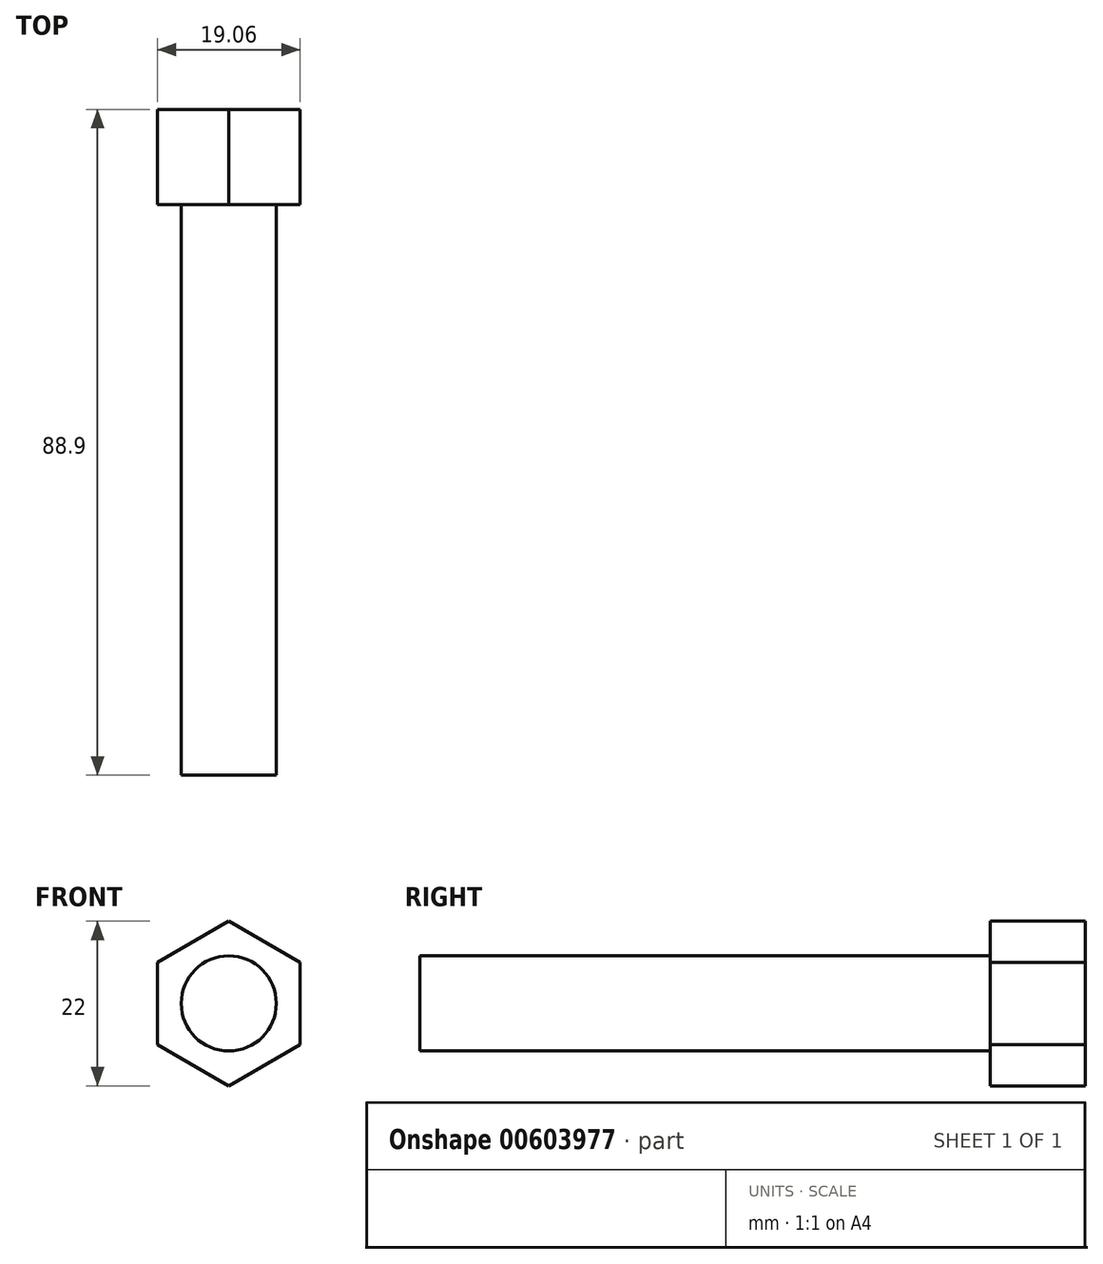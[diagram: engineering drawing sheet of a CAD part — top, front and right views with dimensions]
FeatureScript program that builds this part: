
annotation { "Feature Type Name" : "Feature", "Feature Type Description" : "" }
export const myFeature = defineFeature(function(context is Context, id is Id, definition is map)
    precondition{}
    {
        {
            var Q0;
            Q0=qCreatedBy(makeId("Front.planeOp"),FACE);
            var sketch = newSketch(context, id + "F0", { "sketchPlane" : qUnion([Q0])});
            skCircle(sketch, "E0", {"center": v(0, 0) * mm, "radius": 6.35 * mm});
            skSolve(sketch);
        }
        {
            var Q0;
            Q0 = qSketchRegion(id + "F0", true);
            extrude(context, id + "F1", {"entities" : qUnion([Q0]), "depth" : 88.9 * mm, "offsetDistance" : 25.4 * mm});
        }
        {
            var Q0;
            Q0=qCreatedBy(makeId("Front.planeOp"),FACE);
            var sketch = newSketch(context, id + "F2", { "sketchPlane" : qUnion([Q0])});
            skCircle(sketch, "E1.cCircle", {"center": v(0, 0) * mm, "radius": 9.53 * mm, "construction": true});
            skLineSegment(sketch, "E1.0", {"start": v(-9.53, -5.5) * mm, "end": v(-9.53, 5.5) * mm});
            skLineSegment(sketch, "E1.1", {"start": v(-9.52, 5.5) * mm, "end": v(0, 11) * mm});
            skLineSegment(sketch, "E1.2", {"start": v(0, 11) * mm, "end": v(9.52, 5.5) * mm});
            skLineSegment(sketch, "E1.3", {"start": v(9.52, 5.5) * mm, "end": v(9.53, -5.5) * mm});
            skLineSegment(sketch, "E1.4", {"start": v(9.53, -5.5) * mm, "end": v(0, -11) * mm});
            skLineSegment(sketch, "E1.5", {"start": v(0, -11) * mm, "end": v(-9.52, -5.5) * mm});
            skPoint(sketch, "E1.0.midPoint", {"position": v(-9.53, 0) * mm});
            skSolve(sketch);
        }
        {
            var Q0;
            Q0 = qSketchRegion(id + "F2", true);
            extrude(context, id + "F3", {"entities" : qUnion([Q0]), "operationType" : NewBodyOperationType.ADD, "depth" : 12.7 * mm, "offsetDistance" : 25.4 * mm});
        }
    });
